# Revit family: Haworth_Epure_ManagerDesk_EU_PRELIMINARY
name_source: partatom
category: Furniture
units: mm (PartAtom-declared; Revit-internal decimal feet)

## family parameters
Always vertical = Yes
Cut with Voids When Loaded = No
OmniClass Number = 23.40.70.14.64.11
OmniClass Title = Office Furniture
Room Calculation Point = No
Shared = No
Work Plane-Based = No

## types (4) — shared parameters
Actual Depth = 100 cm
Actual Height = 73 cm
Assembly Code = E2020200
Description = Haworth - Epure - Manager Desk
Flip Top Finish = Haworth _ Paint _ Metallic Silver
Leg Height = 70 cm
Manufacturer = Haworth
Model = EUMAXX10
Revision Number = 1
Size = Verify Final Dim.w/ Haworth
Trim Finish = Haworth _ Metal _ Structured White EC
URL = https://www.haworth.com
URL - Product = https://www.haworth.com
Warranty = http://www.haworth.com

## per-type parameters (varying)
| type | Accessory Kit | Actual Width | Flip Top Cable Outlet | Large | No Accessory Kit | Round Cable Outlet | Rounded Corners | Small | Squared Corners |
| 200 x 100 - squared | No | 200 cm | No | Yes | Yes | No | No | No | Yes |
| 200 x 100 - rounded | Yes | 200 cm | No | Yes | No | Yes | Yes | No | No |
| 180 x 100 - rounded | No | 180 cm | No | No | Yes | No | Yes | Yes | No |
| 180 x 100 - squared | Yes | 180 cm | Yes | No | No | No | No | Yes | Yes |

type visibility flags: 4 boolean params named "<type name>" — each type sets only its own to Yes (folded from table)

## geometry (parser evidence)
native form markers: Sweep x10
no freeform markers — native parametric forms only
